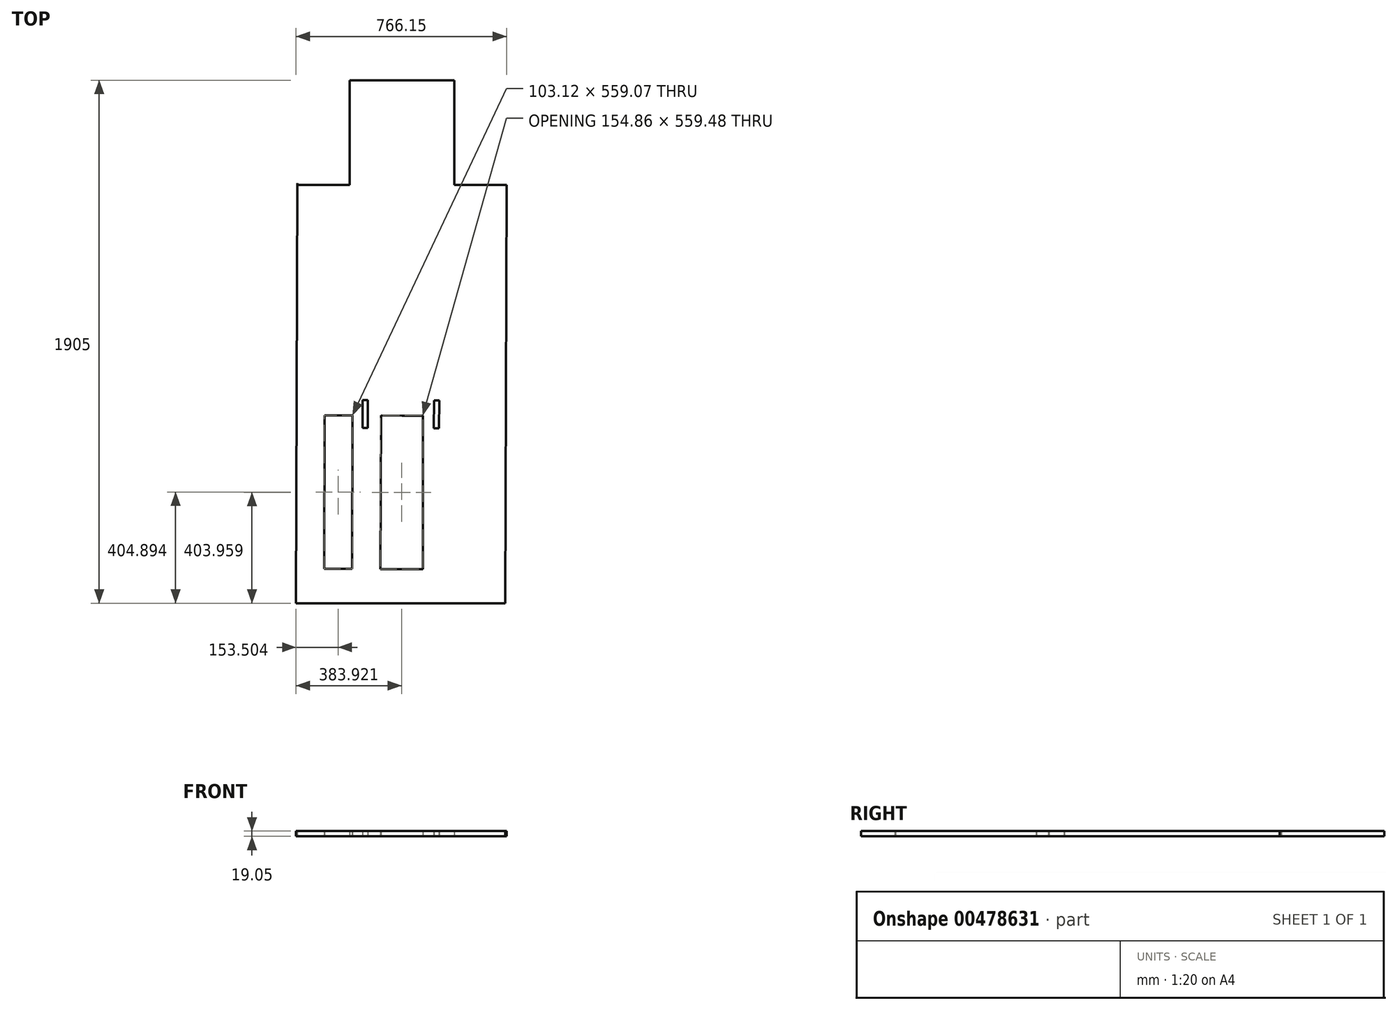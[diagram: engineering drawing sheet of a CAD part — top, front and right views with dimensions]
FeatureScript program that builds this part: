
annotation { "Feature Type Name" : "Feature", "Feature Type Description" : "" }
export const myFeature = defineFeature(function(context is Context, id is Id, definition is map)
    precondition{}
    {
        {
            var Q0;
            Q0=qCreatedBy(makeId("Top.planeOp"),FACE);
            var sketch = newSketch(context, id + "F0", { "sketchPlane" : qUnion([Q0])});
            skLineSegment(sketch, "E0.top", {"start": v(46.65, -124.98) * mm, "end": v(808.65, -124.98) * mm});
            skLineSegment(sketch, "E1", {"start": v(50.82, 1405.35) * mm, "end": v(46.65, -124.98) * mm});
            skLineSegment(sketch, "E2", {"start": v(148.6, 0.65) * mm, "end": v(250.2, 0.38) * mm});
            skLineSegment(sketch, "E3", {"start": v(148.6, 0.65) * mm, "end": v(150.12, 559.45) * mm});
            skLineSegment(sketch, "E4", {"start": v(150.12, 559.45) * mm, "end": v(251.72, 559.17) * mm});
            skLineSegment(sketch, "E5", {"start": v(47.98, 364.3) * mm, "end": v(149.58, 364.02) * mm});
            skLineSegment(sketch, "E6", {"start": v(251.72, 559.17) * mm, "end": v(250.2, 0.38) * mm});
            skLineSegment(sketch, "E7.MirrorCS", {"start": v(713.49, 557.14) * mm, "end": v(611.89, 557.59) * mm});
            skLineSegment(sketch, "E8.MirrorCS", {"start": v(607.46, 557.6) * mm, "end": v(605, -1.2) * mm});
            skLineSegment(sketch, "E9.MirrorCS", {"start": v(706.6, -1.65) * mm, "end": v(709.06, 557.15) * mm});
            skLineSegment(sketch, "E10.MirrorCS", {"start": v(706.6, -1.65) * mm, "end": v(605, -1.2) * mm});
            skLineSegment(sketch, "E11", {"start": v(611.89, 557.59) * mm, "end": v(251.72, 559.17) * mm, "construction": true});
            skLineSegment(sketch, "E12", {"start": v(431.8, 558.38) * mm, "end": v(355.6, 558.72) * mm});
            skLineSegment(sketch, "E13", {"start": v(355.6, 558.72) * mm, "end": v(431.8, 558.38) * mm});
            skLineSegment(sketch, "E14", {"start": v(431.8, 558.38) * mm, "end": v(508, 558.04) * mm});
            skLineSegment(sketch, "E15", {"start": v(355.6, 558.72) * mm, "end": v(353.14, -0.41) * mm});
            skLineSegment(sketch, "E16", {"start": v(353.14, -0.41) * mm, "end": v(429.34, -0.41) * mm});
            skLineSegment(sketch, "E17", {"start": v(429.34, -0.41) * mm, "end": v(508, -0.76) * mm});
            skLineSegment(sketch, "E18", {"start": v(508, -0.76) * mm, "end": v(508, 558.04) * mm});
            skLineSegment(sketch, "E19.top", {"start": v(50.82, 1399.02) * mm, "end": v(812.8, 1399.02) * mm});
            skLineSegment(sketch, "E19.right", {"start": v(808.65, -124.98) * mm, "end": v(812.8, 1399.02) * mm});
            skPoint(sketch, "E20", {"position": v(622.3, 1399.02) * mm});
            skPoint(sketch, "E21", {"position": v(241.3, 1399.02) * mm});
            skLineSegment(sketch, "E22.bottom", {"start": v(241.3, 1399.02) * mm, "end": v(622.3, 1399.02) * mm});
            skLineSegment(sketch, "E22.top", {"start": v(241.3, 1780.02) * mm, "end": v(622.3, 1780.02) * mm});
            skLineSegment(sketch, "E22.left", {"start": v(241.3, 1399.02) * mm, "end": v(241.3, 1780.02) * mm});
            skLineSegment(sketch, "E22.right", {"start": v(622.3, 1399.02) * mm, "end": v(622.3, 1780.02) * mm});
            skLineSegment(sketch, "E23", {"start": v(50.82, 1399.02) * mm, "end": v(50.82, 1405.35) * mm});
            skLineSegment(sketch, "E24.bottom", {"start": v(289.07, 615.42) * mm, "end": v(308.12, 615.42) * mm});
            skLineSegment(sketch, "E24.top", {"start": v(289.07, 513.82) * mm, "end": v(308.12, 513.82) * mm});
            skLineSegment(sketch, "E24.left", {"start": v(289.07, 615.42) * mm, "end": v(289.07, 513.82) * mm});
            skLineSegment(sketch, "E24.right", {"start": v(308.12, 615.42) * mm, "end": v(308.12, 513.82) * mm});
            skLineSegment(sketch, "E25.MirrorCS", {"start": v(549.42, 614.36) * mm, "end": v(548.52, 512.76) * mm});
            skLineSegment(sketch, "E26.MirrorCS", {"start": v(567.57, 512.6) * mm, "end": v(548.52, 512.76) * mm});
            skLineSegment(sketch, "E27.MirrorCS", {"start": v(568.47, 614.19) * mm, "end": v(567.57, 512.6) * mm});
            skLineSegment(sketch, "E28.MirrorCS", {"start": v(568.47, 614.19) * mm, "end": v(549.42, 614.36) * mm});
            skPoint(sketch, "E29.centerSnap0", {"position": v(428.29, 1594.18) * mm});
            skLineSegment(sketch, "E30", {"start": v(427.65, -124.98) * mm, "end": v(431.8, 1399.02) * mm, "construction": true});
            skSolve(sketch);
        }
        {
            var Q0;
            {var subQ0=sQuery(id+"F0.wireOp",EDGE,"E22.bottom");Q0=makeQuery(id+"F0.imprint","IMPRINT",FACE,{"disambiguationData":[TD([[makeQuery(id+"F0.imprint","IMPRINT",EDGE,{"derivedFrom":subQ0}),1.0]])]});}
            var Q1;
            {var subQ1=sQuery(id+"F0.wireOp",EDGE,"E22.top");Q1=makeQuery(id+"F0.imprint","IMPRINT",FACE,{"disambiguationData":[TD([[makeQuery(id+"F0.imprint","IMPRINT",EDGE,{"derivedFrom":subQ1}),-1.0]])]});}
            var Q2;
            {var subQ17=sQuery(id+"F0.wireOp",EDGE,"E2");Q2=makeQuery(id+"F0.imprint","IMPRINT",FACE,{"disambiguationData":[TD([[makeQuery(id+"F0.imprint","IMPRINT",EDGE,{"derivedFrom":subQ17}),-1.0]])]});}
            extrude(context, id + "F1", {"entities" : qUnion([Q0, Q1, Q2]), "depth" : 19.05 * mm, "offsetDistance" : 25.4 * mm});
        }
    });
